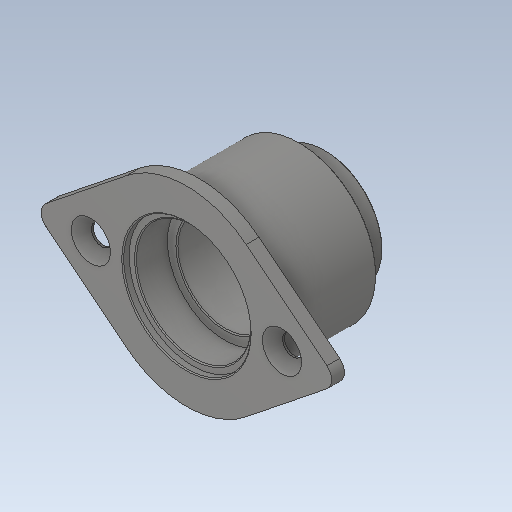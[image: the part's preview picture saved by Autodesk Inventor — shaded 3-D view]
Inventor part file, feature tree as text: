
AUTODESK INVENTOR PART (.ipt)
format: ipt  version: 2020 (Build 240168000, 168)  size: 178,688 bytes
history: native  units: in
note: dims shown in document units (in); Inventor stores cm internally (conversion verified against a paired STEP export)
features: chamfer x1
ambient origin geometry x8: Origin, YZ Plane, XZ Plane, XY Plane, X Axis, Y Axis, Z Axis, Center Point
bodies: Solid1 (feature_tree)
feature tree (1):
  chamfer  "Chamfer1"  [1 undecoded]
note: 1 required parameter value undecoded (feature->parameter linkage not recoverable at this tier; creation-order binding heuristic only, values carry confidence <= 0.55)
